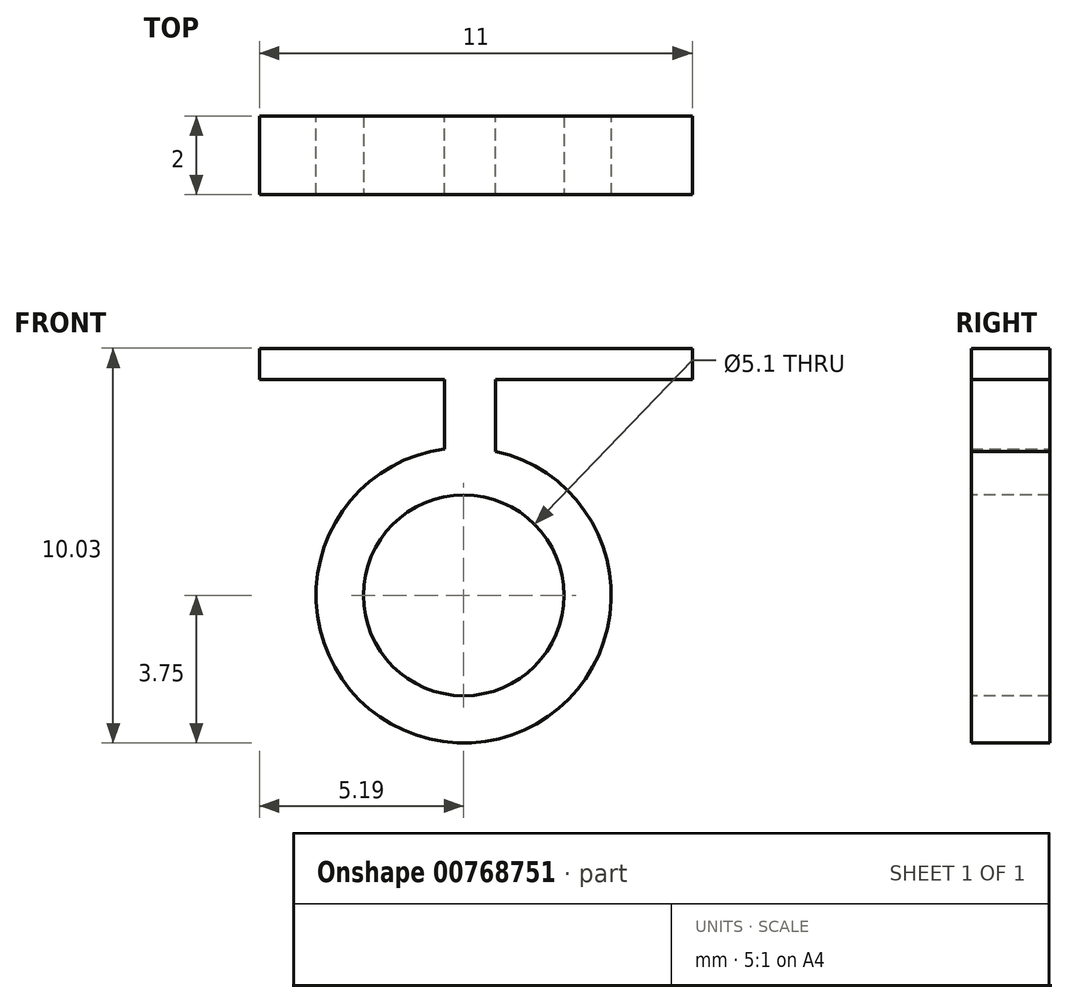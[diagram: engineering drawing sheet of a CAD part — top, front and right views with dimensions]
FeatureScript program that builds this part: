
annotation { "Feature Type Name" : "Feature", "Feature Type Description" : "" }
export const myFeature = defineFeature(function(context is Context, id is Id, definition is map)
    precondition{}
    {
        {
            var Q0;
            Q0=qCreatedBy(makeId("Front.planeOp"),FACE);
            var sketch = newSketch(context, id + "F0", { "sketchPlane" : qUnion([Q0])});
            skCircle(sketch, "E0", {"center": v(0, 0) * mm, "radius": 3.75 * mm});
            skSolve(sketch);
        }
        {
            var Q0;
            Q0 = qSketchRegion(id + "F0", true);
            extrude(context, id + "F1", {"entities" : qUnion([Q0]), "depth" : 2 * mm, "offsetDistance" : 25 * mm});
        }
        {
            var Q0;
            Q0=qCreatedBy(makeId("Front.planeOp"),FACE);
            var sketch = newSketch(context, id + "F2", { "sketchPlane" : qUnion([Q0])});
            skCircle(sketch, "E1", {"center": v(0, 0) * mm, "radius": 2.55 * mm});
            skSolve(sketch);
        }
        {
            var Q0;
            Q0 = qSketchRegion(id + "F2", true);
            extrude(context, id + "F3", {"entities" : qUnion([Q0]), "operationType" : NewBodyOperationType.REMOVE, "oppositeDirection" : true, "depth" : 25 * mm, "offsetDistance" : 25 * mm});
        }
        {
            var Q0;
            Q0=makeQuery(id+"F1.opExtrude","CAP_FACE",FACE,{"disambiguationData":[OSD([sQuery(id+"F0.wireOp",EDGE,"E0")])],"isStart":false});
            var sketch = newSketch(context, id + "F4", { "sketchPlane" : qUnion([Q0])});
            skCircle(sketch, "E2", {"center": v(0, 0) * mm, "radius": 2.55 * mm});
            skSolve(sketch);
        }
        {
            var Q0;
            Q0=makeQuery(id+"F4.imprint","IMPRINT",FACE,{"disambiguationData":[TD([[makeQuery(id+"F4.imprint","IMPRINT",EDGE,{"derivedFrom":sQuery(id+"F4.wireOp",EDGE,"E2")}),1.0]])]});
            extrude(context, id + "F5", {"entities" : qUnion([Q0]), "operationType" : NewBodyOperationType.REMOVE, "oppositeDirection" : true, "depth" : 25 * mm, "offsetDistance" : 25 * mm});
        }
        {
            var Q0;
            Q0=makeQuery(id+"F1.opExtrude","CAP_FACE",FACE,{"disambiguationData":[OSD([sQuery(id+"F0.wireOp",EDGE,"E0")])],"isStart":true});
            var sketch = newSketch(context, id + "F6", { "sketchPlane" : qUnion([Q0])});
            skLineSegment(sketch, "E3.bottom", {"start": v(-0.81, 3.46) * mm, "end": v(0.49, 3.46) * mm});
            skLineSegment(sketch, "E3.top", {"start": v(-0.81, 6.28) * mm, "end": v(0.49, 6.28) * mm});
            skLineSegment(sketch, "E3.left", {"start": v(-0.81, 3.46) * mm, "end": v(-0.81, 6.28) * mm});
            skLineSegment(sketch, "E3.right", {"start": v(0.49, 3.46) * mm, "end": v(0.49, 6.28) * mm});
            skSolve(sketch);
        }
        {
            var Q0;
            Q0 = qSketchRegion(id + "F6", true);
            extrude(context, id + "F7", {"entities" : qUnion([Q0]), "operationType" : NewBodyOperationType.ADD, "oppositeDirection" : true, "depth" : 2 * mm, "offsetDistance" : 25 * mm});
        }
        {
            var Q0;
            Q0=makeQuery(id+"F7.opExtrude","SWEPT_FACE",FACE,{"disambiguationData":[OSD([sQuery(id+"F6.wireOp",EDGE,"E3.left")])]});
            var sketch = newSketch(context, id + "F8", { "sketchPlane" : qUnion([Q0])});
            skLineSegment(sketch, "E4.bottom", {"start": v(-2, 6.28) * mm, "end": v(0, 6.28) * mm});
            skLineSegment(sketch, "E4.top", {"start": v(-2, 5.49) * mm, "end": v(0, 5.49) * mm});
            skLineSegment(sketch, "E4.left", {"start": v(-2, 6.28) * mm, "end": v(-2, 5.49) * mm});
            skLineSegment(sketch, "E4.right", {"start": v(0, 6.28) * mm, "end": v(0, 5.49) * mm});
            skSolve(sketch);
        }
        {
            var Q0;
            Q0 = qSketchRegion(id + "F8", true);
            extrude(context, id + "F9", {"entities" : qUnion([Q0]), "operationType" : NewBodyOperationType.ADD, "depth" : 5 * mm, "offsetDistance" : 25 * mm, "hasSecondDirection" : true, "secondDirectionOppositeDirection" : true, "secondDirectionDepth" : 6 * mm});
        }
    });
